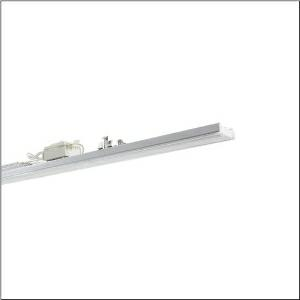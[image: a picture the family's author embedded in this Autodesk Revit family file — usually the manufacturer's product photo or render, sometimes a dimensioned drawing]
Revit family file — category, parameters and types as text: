
# Revit family: licross_r__11_recessed_mo_51tl117n485g_1672
name_source: partatom
category: Lighting Fixtures
units: mm (PartAtom-declared; Revit-internal decimal feet)

## family parameters
Cut with Voids When Loaded = No
Host = Face
Light Source = No
Part Type = Normal
Room Calculation Point = No
Round Connector Dimension = Use Diameter
Shared = No

## types (1)
- Licross® 11 Recessed MO (1 x LED, 8810 lm, 48.5 W, 4000K)
    Apparent Load = 49 VA
    CIE Flux Codes = 89 96 99 100 100
    Color Rendering = 80
    Color Temperature = 4000K
    Default Elevation = 1800 mm
    Description = Licross® 11 Recessed MO, luminaire insert, of sheet steel, coil coated, white, length: 1.500mm, width: 66mm, height: 67mm, LED rated luminous flux: 8.820lm, light colour: 840, control gear: ON/OFF, with plug, 3-pole, with phase selection, mains connection: 220..240V, AC, 50/60Hz, rated input power: 49W, internal wiring halogen-free, primary light control with lens, of plastic, primary optical cover: cover, of PMMA, light emission: direct distribution, primary light characteristic: symmetric, protection rating (complete): IP40, insulation class (complete): insulation class I (protective earthing), certification: CE, ENEC, VDE, UKCA, protection symbol: D if used in an environment without relevant dust loads with corresponding accessories, impact resistance: IK06, permissible ambient temperature for indoor applications: -35..+35°C, corresponds to IFS (International Featured Standards) requirements for safety and quality in the food industry, reducing of maximum allowable ambient temperature of 5°C with ceiling mounting, packaging unit: 1 piece
    Height = 58 mm
    Lamp = 1 x LED
    Lamp Light Flux = 8810 lm
    Lamp Power = 48.5 W
    Lamp count = 1
    Length = 1500 mm
    Luminous efficacy = 182 lm/W
    Manufacturer = Siteco
    ModVariant = No
    Model = 51TL117N485G
    Mounting Place = Ceiling
    Mounting Type = Pendant
    Number of Poles = 1
    OnlyDefault = Yes
    Power Factor = 1
    Product Name = Licross® 11 Recessed MO
    Product group = luminaire insert | ceiling pendant
    ProductGroupID = 902
    Protection Class = Protection class I
    Protection Degree = IP 40
    RLX_Detail_Level = 1
    RLX_Emergency_Light_Flux = 0 lm
    RLX_Emergency_Type = 0
    RLX_Emergency_Type_DB = No
    RlxData = <blob elided: 20813 chars, md5=6274aaa3>
    Socket = socket
    Standby Power = 0 W
    System Light Flux = 8810 lm
    System Power = 49 W
    Type Comments = Product without accessories
    Type Image = l_1296930.jpg
    URL = http://relux.com
    VarID = ---
    Voltage = 0 V
    Weight = 0.00 kg
    Width = 66 mm

## geometry (parser evidence)
native form markers: Blend x4, Sweep x12
no freeform markers — native parametric forms only
